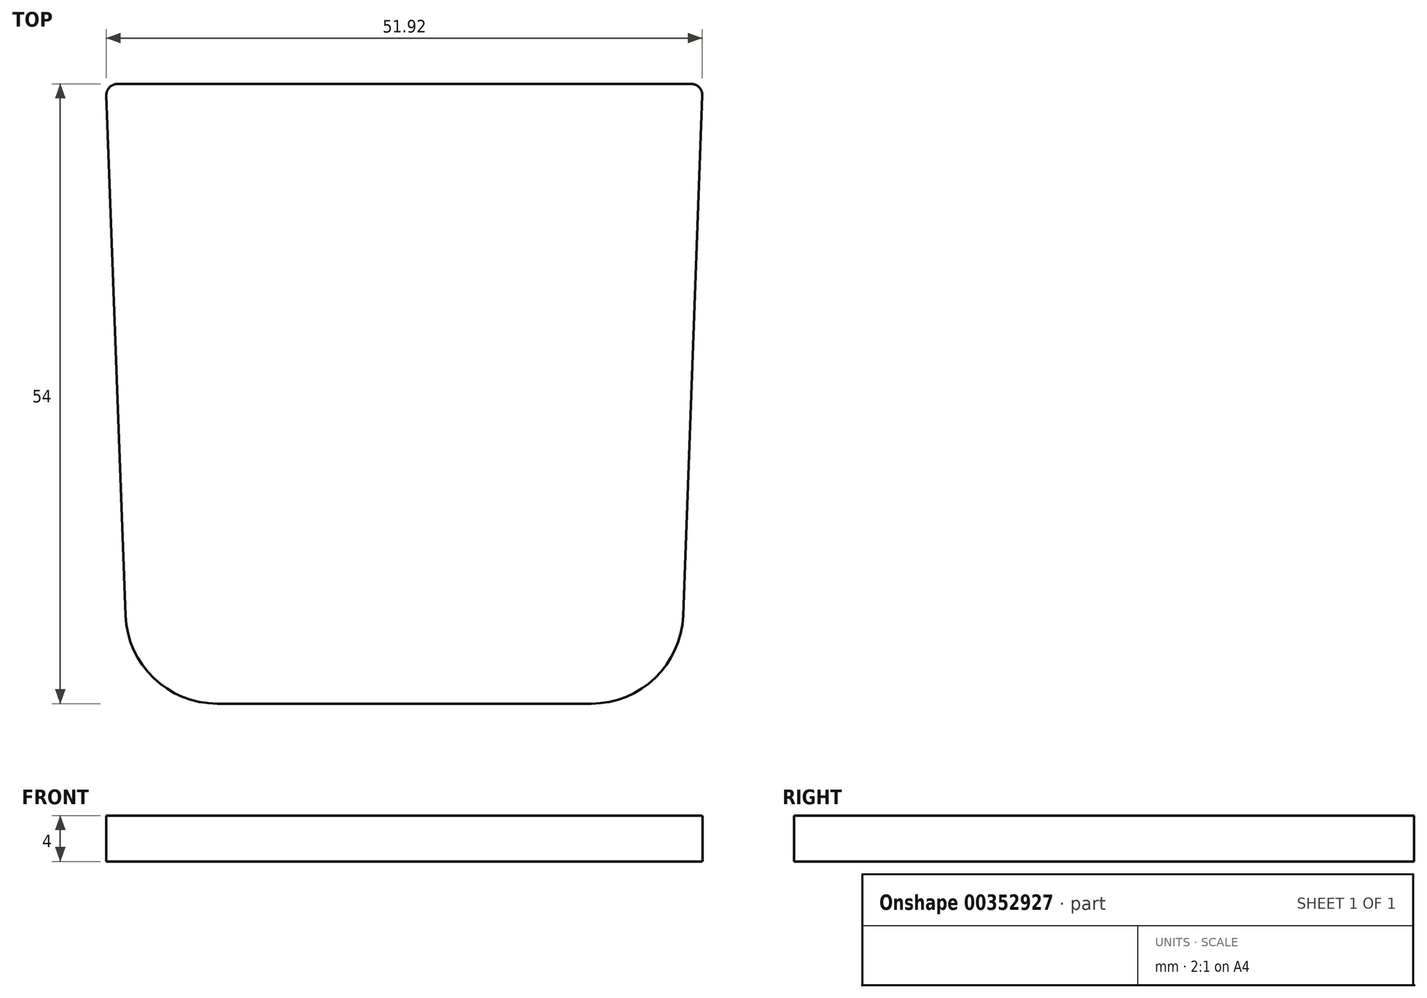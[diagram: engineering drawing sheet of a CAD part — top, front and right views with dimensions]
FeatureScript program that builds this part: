
annotation { "Feature Type Name" : "Feature", "Feature Type Description" : "" }
export const myFeature = defineFeature(function(context is Context, id is Id, definition is map)
    precondition{}
    {
        {
            var Q0;
            Q0=qCreatedBy(makeId("Top.planeOp"),FACE);
            var sketch = newSketch(context, id + "F0", { "sketchPlane" : qUnion([Q0])});
            skLineSegment(sketch, "E0", {"start": v(1.04, 0) * mm, "end": v(50.96, 0) * mm});
            skLineSegment(sketch, "E1", {"start": v(9.7, -54) * mm, "end": v(42.3, -54) * mm});
            skLineSegment(sketch, "E2", {"start": v(0.04, -1.04) * mm, "end": v(1.71, -46.3) * mm});
            skLineSegment(sketch, "E3", {"start": v(50.29, -46.3) * mm, "end": v(51.96, -1.04) * mm});
            skPoint(sketch, "E4.visualSharp", {"position": v(2, -54) * mm});
            skArc(sketch, "E4.filletArc", {"start": v(1.71, -46.3) * mm, "mid": v(4.16, -51.76) * mm, "end": v(9.7, -54) * mm});
            skPoint(sketch, "E5.visualSharp", {"position": v(50, -54) * mm});
            skArc(sketch, "E5.filletArc", {"start": v(42.3, -54) * mm, "mid": v(47.84, -51.76) * mm, "end": v(50.29, -46.3) * mm});
            skPoint(sketch, "E6.visualSharp", {"position": v(0, 0) * mm});
            skArc(sketch, "E6.filletArc", {"start": v(1.04, 0) * mm, "mid": v(0.32, -0.3) * mm, "end": v(0.04, -1.04) * mm});
            skPoint(sketch, "E7.visualSharp", {"position": v(52, 0) * mm});
            skArc(sketch, "E7.filletArc", {"start": v(51.96, -1.04) * mm, "mid": v(51.68, -0.3) * mm, "end": v(50.96, 0) * mm});
            skSolve(sketch);
        }
        {
            var Q0;
            Q0=makeQuery(id+"F0.imprint","IMPRINT",FACE,{"disambiguationData":[TD([[makeQuery(id+"F0.imprint","IMPRINT",EDGE,{"derivedFrom":sQuery(id+"F0.wireOp",EDGE,"E0")}),-1.0]])]});
            extrude(context, id + "F1", {"entities" : qUnion([Q0]), "depth" : 4 * mm});
        }
    });
